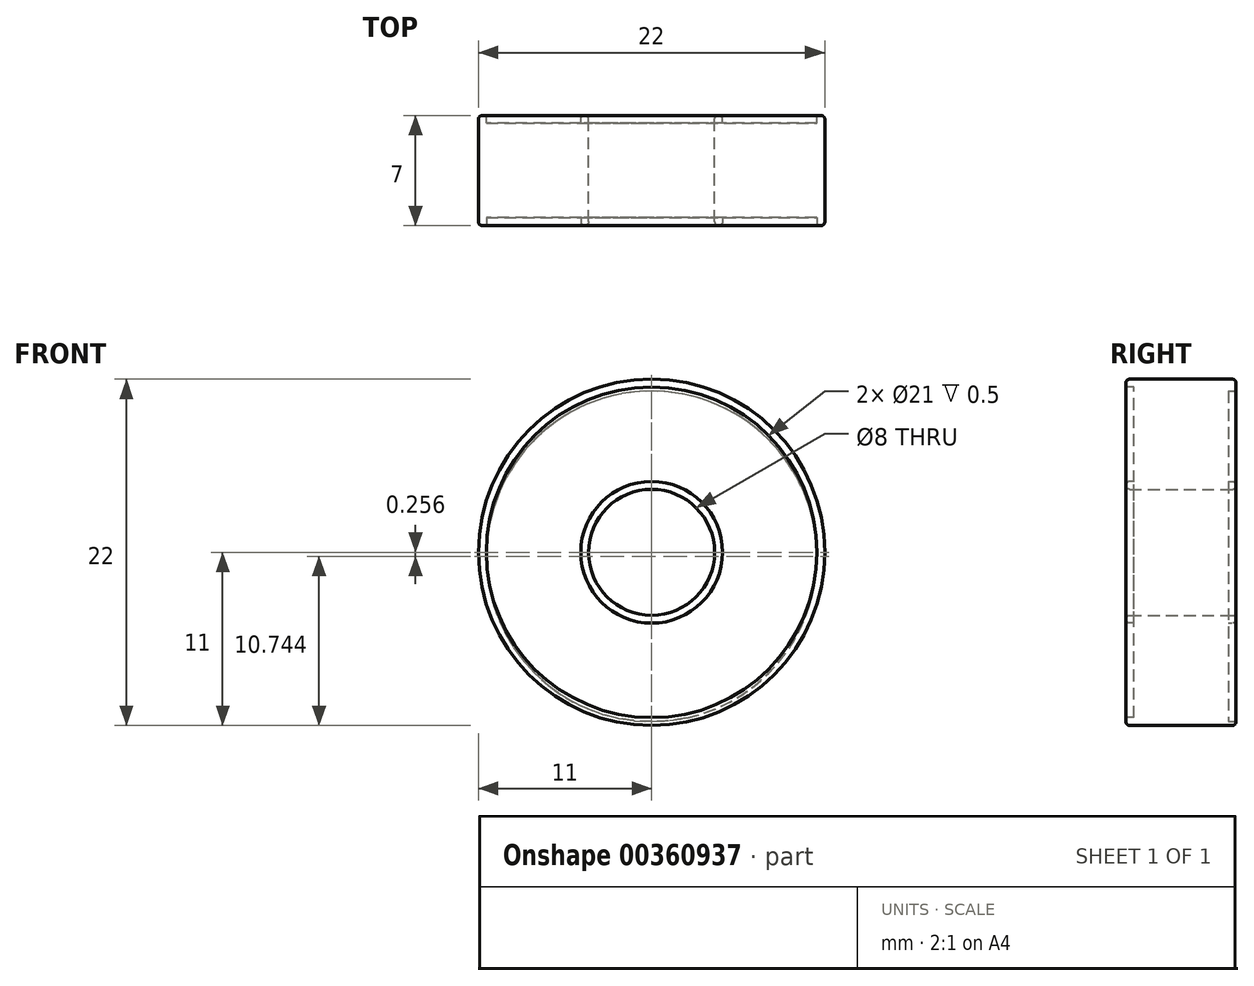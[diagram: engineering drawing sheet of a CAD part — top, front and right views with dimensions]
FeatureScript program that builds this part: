
annotation { "Feature Type Name" : "Feature", "Feature Type Description" : "" }
export const myFeature = defineFeature(function(context is Context, id is Id, definition is map)
    precondition{}
    {
        {
            var Q0;
            Q0=qCreatedBy(makeId("Front.planeOp"),FACE);
            var sketch = newSketch(context, id + "F0", { "sketchPlane" : qUnion([Q0])});
            skCircle(sketch, "E0", {"center": v(0, 0) * mm, "radius": 4 * mm});
            skCircle(sketch, "E1", {"center": v(0, 0) * mm, "radius": 11 * mm});
            skSolve(sketch);
        }
        {
            var Q0;
            Q0 = qSketchRegion(id + "F0", true);
            extrude(context, id + "F1", {"entities" : qUnion([Q0]), "depth" : 7 * mm});
        }
        {
            var Q0;
            Q0=makeQuery(id+"F1.opExtrude","CAP_FACE",FACE,{"disambiguationData":[OSD([sQuery(id+"F0.wireOp",EDGE,"E0"),sQuery(id+"F0.wireOp",EDGE,"E1")])],"isStart":false});
            var sketch = newSketch(context, id + "F2", { "sketchPlane" : qUnion([Q0])});
            skCircle(sketch, "E2", {"center": v(0, 0) * mm, "radius": 4.5 * mm});
            skCircle(sketch, "E3", {"center": v(0, 0) * mm, "radius": 10.5 * mm});
            skSolve(sketch);
        }
        {
            var Q0;
            Q0 = qSketchRegion(id + "F2", true);
            extrude(context, id + "F3", {"entities" : qUnion([Q0]), "operationType" : NewBodyOperationType.REMOVE, "oppositeDirection" : true, "depth" : 0.5 * mm});
        }
        {
            var Q0;
            Q0=makeQuery(id+"F1.opExtrude","CAP_FACE",FACE,{"disambiguationData":[OSD([sQuery(id+"F0.wireOp",EDGE,"E0"),sQuery(id+"F0.wireOp",EDGE,"E1")])],"isStart":true});
            var sketch = newSketch(context, id + "F4", { "sketchPlane" : qUnion([Q0])});
            skCircle(sketch, "E4", {"center": v(0, 0) * mm, "radius": 4.5 * mm});
            skCircle(sketch, "E5", {"center": v(0, -0.26) * mm, "radius": 10.5 * mm});
            skSolve(sketch);
        }
        {
            var Q0;
            Q0 = qSketchRegion(id + "F4", true);
            extrude(context, id + "F5", {"entities" : qUnion([Q0]), "operationType" : NewBodyOperationType.REMOVE, "oppositeDirection" : true, "depth" : 0.5 * mm});
        }
        {
            var Q0;
            Q0=makeQuery(id+"F5.boolean.opBoolean","COPY",EDGE,{"derivedFrom":makeQuery(id+"F5.opExtrude","CAP_EDGE",EDGE,{"disambiguationData":[OSD([sQuery(id+"F4.wireOp",EDGE,"E4")])],"isStart":true})});
            var Q1;
            Q1=makeQuery(id+"F1.opExtrude","CAP_EDGE",EDGE,{"disambiguationData":[OSD([sQuery(id+"F0.wireOp",EDGE,"E0")])],"isStart":true});
            var Q2;
            Q2=makeQuery(id+"F5.boolean.opBoolean","COPY",EDGE,{"derivedFrom":makeQuery(id+"F5.opExtrude","CAP_EDGE",EDGE,{"disambiguationData":[OSD([sQuery(id+"F4.wireOp",EDGE,"E5")])],"isStart":true})});
            var Q3;
            Q3=makeQuery(id+"F1.opExtrude","CAP_EDGE",EDGE,{"disambiguationData":[OSD([sQuery(id+"F0.wireOp",EDGE,"E1")])],"isStart":true});
            var Q4;
            Q4=makeQuery(id+"F1.opExtrude","CAP_EDGE",EDGE,{"disambiguationData":[OSD([sQuery(id+"F0.wireOp",EDGE,"E1")])],"isStart":false});
            var Q5;
            Q5=makeQuery(id+"F3.boolean.opBoolean","COPY",EDGE,{"derivedFrom":makeQuery(id+"F3.opExtrude","CAP_EDGE",EDGE,{"disambiguationData":[OSD([sQuery(id+"F2.wireOp",EDGE,"E3")])],"isStart":true})});
            var Q6;
            Q6=makeQuery(id+"F3.boolean.opBoolean","COPY",EDGE,{"derivedFrom":makeQuery(id+"F3.opExtrude","CAP_EDGE",EDGE,{"disambiguationData":[OSD([sQuery(id+"F2.wireOp",EDGE,"E2")])],"isStart":true})});
            var Q7;
            Q7=makeQuery(id+"F1.opExtrude","CAP_EDGE",EDGE,{"disambiguationData":[OSD([sQuery(id+"F0.wireOp",EDGE,"E0")])],"isStart":false});
            fillet(context, id + "F6", {"entities" : qUnion([Q0, Q1, Q2, Q3, Q4, Q5, Q6, Q7]), "radius" : 0.25 * mm, "tangentPropagation" : true, "allowEdgeOverflow" : false});
        }
    });
